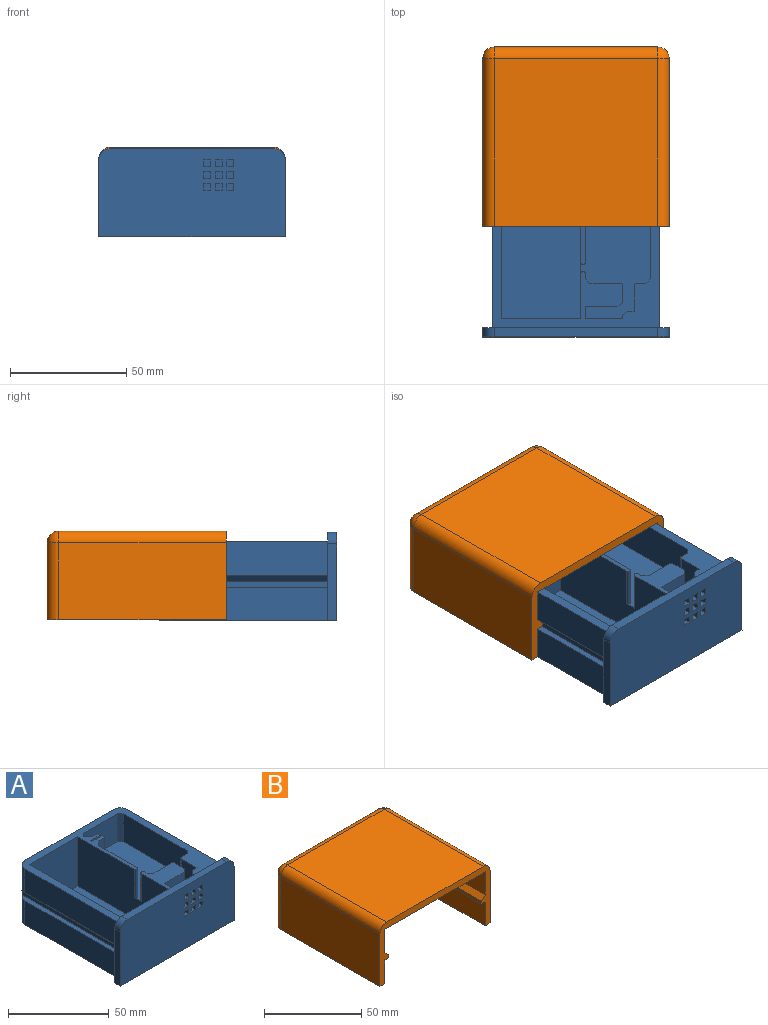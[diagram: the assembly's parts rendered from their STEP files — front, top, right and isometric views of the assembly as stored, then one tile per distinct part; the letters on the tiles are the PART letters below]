
ASSEMBLY  parts=2 mates=1
PART A: 96 faces, bbox 80x76x38 mm
  f0: plane 17x16mm, normal (0,1,0), area 191mm2, adj f11,f12,f34,f41,f42,f43,f44,f45
  f1: plane 80x38mm, normal (0,-1,0), area 2948.3mm2, adj f5,f6,f7,f8,f41,f42,f43,f44
  f2: plane 62x34mm, normal (0,1,0), area 2108mm2, adj f5,f34,f84,f85
  f3: plane 67x14.5mm, normal (-1,0,0), area 971.5mm2, adj f5,f37,f39,f84
  f4: plane 67x14.5mm, normal (1,0,0), area 971.5mm2, adj f5,f36,f39,f85
  f5: plane 80x76mm, normal (0,0,-1), area 5493.3mm2, adj f1,f2,f3,f4,f6,f8,f39,f84
  f6: plane 33x4mm, normal (1,0,0), area 132mm2, adj f1,f5,f39,f86
  f7: plane 70x4mm, normal (0,0,1), area 280mm2, adj f1,f39,f86,f87
  f8: plane 33x4mm, normal (-1,0,0), area 132mm2, adj f1,f5,f39,f87
  f9: plane 67x14.5mm, normal (-1,0,0), area 971.5mm2, adj f34,f39,f84,f94
  f10: plane 17x3mm, normal (0,1,0), area 51mm2, adj f32,f34,f77,f82
  f11: plane 17x1mm, normal (-1,0,0), area 17mm2, adj f0,f34,f77,f82
  f12: plane 17x5mm, normal (1,0,0), area 85mm2, adj f0,f13,f34,f77
  f13: plane 17x14mm, normal (0,-1,0), area 238mm2, adj f12,f34,f77,f81
  f14: plane 17x7mm, normal (1,0,0), area 119mm2, adj f34,f77,f81,f88
  f15: plane 17x13mm, normal (0,1,0), area 221mm2, adj f34,f77,f79,f88
  f16: plane 17x2mm, normal (1,0,0), area 34mm2, adj f34,f77,f79,f89
  f17: plane 64x30mm, normal (-1,0,0), area 1835mm2, adj f18,f20,f34,f40,f77,f89,f90
  f18: plane 34x30mm, normal (0,1,0), area 1020mm2, adj f17,f19,f34,f40
  f19: plane 64x30mm, normal (1,0,0), area 1920mm2, adj f18,f20,f34,f40
  f20: plane 34x30mm, normal (0,-1,0), area 1020mm2, adj f17,f19,f34,f40
  f21: plane 27x17mm, normal (1,0,0), area 459mm2, adj f34,f77,f90,f93
  f22: plane 17x4mm, normal (0,-1,0), area 68mm2, adj f23,f34,f77,f93
  f23: plane 17x2mm, normal (1,0,0), area 34mm2, adj f22,f24,f34,f77
  f24: plane 17x7mm, normal (0,1,0), area 119mm2, adj f23,f25,f34,f77
  f25: plane 17x1mm, normal (1,0,0), area 17mm2, adj f24,f26,f34,f77
  f26: plane 17x7mm, normal (0,-1,0), area 119mm2, adj f25,f27,f34,f77
  f27: plane 17x2mm, normal (1,0,0), area 34mm2, adj f26,f28,f34,f77
  f28: plane 17x4mm, normal (0,1,0), area 68mm2, adj f27,f34,f77,f92
  f29: plane 24x17mm, normal (0,-1,0), area 408mm2, adj f34,f77,f78,f83
  f30: plane 45x17mm, normal (-1,0,0), area 765mm2, adj f34,f77,f78,f80
  f31: plane 17x4mm, normal (0,1,0), area 68mm2, adj f34,f77,f80,f91
  f32: plane 17x11mm, normal (-1,0,0), area 187mm2, adj f10,f34,f77,f91
  f33: plane 67x14.5mm, normal (1,0,0), area 971.5mm2, adj f34,f39,f85,f95
  f34: plane 72x72mm, normal (0,0,1), area 1519mm2, adj f0,f2,f9,f10,f11,f12,f13,f14
  f35: plane 71.42x2.33mm, normal (1,0,0), area 166.7mm2, adj f36,f39,f85,f95
  f36: plane 71.42x2.67mm, normal (0,0,1), area 187.1mm2, adj f4,f35,f39,f85
  f37: plane 71.42x2.67mm, normal (0,0,1), area 187.1mm2, adj f3,f38,f39,f84
  f38: plane 71.42x2.33mm, normal (-1,0,0), area 166.7mm2, adj f37,f39,f84,f94
  f39: plane 80x38mm, normal (0,1,0), area 600.8mm2, adj f3,f4,f5,f6,f7,f8,f9,f33
  f40: plane 64x34mm, normal (0,0,1), area 2176mm2, adj f17,f18,f19,f20
  f41: plane 8x3mm, normal (0,0,-1), area 24mm2, adj f0,f1,f42,f44
  f42: plane 8x3mm, normal (-1,0,0), area 24mm2, adj f0,f1,f41,f43
  f43: plane 8x3mm, normal (0,0,1), area 24mm2, adj f0,f1,f42,f44
  f44: plane 8x3mm, normal (1,0,0), area 24mm2, adj f0,f1,f41,f43
  f45: plane 8x3mm, normal (0,0,-1), area 24mm2, adj f0,f1,f46,f48
  f46: plane 8x3mm, normal (-1,0,0), area 24mm2, adj f0,f1,f45,f47
  f47: plane 8x3mm, normal (0,0,1), area 24mm2, adj f0,f1,f46,f48
  f48: plane 8x3mm, normal (1,0,0), area 24mm2, adj f0,f1,f45,f47
  f49: plane 8x3mm, normal (0,0,-1), area 24mm2, adj f0,f1,f50,f52
  f50: plane 8x3mm, normal (-1,0,0), area 24mm2, adj f0,f1,f49,f51
  f51: plane 8x3mm, normal (0,0,1), area 24mm2, adj f0,f1,f50,f52
  f52: plane 8x3mm, normal (1,0,0), area 24mm2, adj f0,f1,f49,f51
  f53: plane 8x3mm, normal (0,0,-1), area 24mm2, adj f0,f1,f54,f55
  f54: plane 8x3mm, normal (1,0,0), area 24mm2, adj f0,f1,f53,f56
  f55: plane 8x3mm, normal (-1,0,0), area 24mm2, adj f0,f1,f53,f56
  f56: plane 8x3mm, normal (0,0,1), area 24mm2, adj f0,f1,f54,f55
  f57: plane 8x3mm, normal (0,0,-1), area 24mm2, adj f0,f1,f58,f60
  f58: plane 8x3mm, normal (-1,0,0), area 24mm2, adj f0,f1,f57,f59
  f59: plane 8x3mm, normal (0,0,1), area 24mm2, adj f0,f1,f58,f60
  f60: plane 8x3mm, normal (1,0,0), area 24mm2, adj f0,f1,f57,f59
  f61: plane 8x3mm, normal (0,0,-1), area 24mm2, adj f0,f1,f62,f63
  f62: plane 8x3mm, normal (1,0,0), area 24mm2, adj f0,f1,f61,f64
  f63: plane 8x3mm, normal (-1,0,0), area 24mm2, adj f0,f1,f61,f64
  f64: plane 8x3mm, normal (0,0,1), area 24mm2, adj f0,f1,f62,f63
  f65: plane 8x3mm, normal (0,0,-1), area 24mm2, adj f0,f1,f66,f68
  f66: plane 8x3mm, normal (-1,0,0), area 24mm2, adj f0,f1,f65,f67
  f67: plane 8x3mm, normal (0,0,1), area 24mm2, adj f0,f1,f66,f68
  f68: plane 8x3mm, normal (1,0,0), area 24mm2, adj f0,f1,f65,f67
  f69: plane 8x3mm, normal (-1,0,0), area 24mm2, adj f0,f1,f70,f72
  f70: plane 8x3mm, normal (0,0,1), area 24mm2, adj f0,f1,f69,f71
  f71: plane 8x3mm, normal (1,0,0), area 24mm2, adj f0,f1,f70,f72
  f72: plane 8x3mm, normal (0,0,-1), area 24mm2, adj f0,f1,f69,f71
  f73: plane 8x3mm, normal (-1,0,0), area 24mm2, adj f0,f1,f74,f76
  f74: plane 8x3mm, normal (0,0,1), area 24mm2, adj f0,f1,f73,f75
  f75: plane 8x3mm, normal (1,0,0), area 24mm2, adj f0,f1,f74,f76
  f76: plane 8x3mm, normal (0,0,-1), area 24mm2, adj f0,f1,f73,f75
  f77: plane 64x30mm, normal (0,0,1), area 1478.3mm2, adj f0,f10,f11,f12,f13,f14,f15,f16
  f78: plane 17x2mm, normal (-0.71,-0.71,0), area 48.1mm2, adj f29,f30,f34,f77
  f79: plane 17x2mm, normal (0.71,0.71,0), area 48.1mm2, adj f15,f16,f34,f77
  f80: plane 17x2mm, normal (-0.71,0.71,0), area 48.1mm2, adj f30,f31,f34,f77
  f81: plane 17x2mm, normal (0.71,-0.71,0), area 48.1mm2, adj f13,f14,f34,f77
  f82: plane 17x2mm, normal (-0.71,0.71,0), area 48.1mm2, adj f10,f11,f34,f77
  f83: plane 17x2mm, normal (0.71,-0.71,0), area 48.1mm2, adj f29,f34,f77,f92
  f84: cylinder r=5mm len=34mm, axis (0,0,-1), area 244.9mm2, adj f2,f3,f5,f9,f34,f37,f38,f94
  f85: cylinder r=5mm len=34mm, axis (0,0,1), area 244.9mm2, adj f2,f4,f5,f33,f34,f35,f36,f95
  f86: cylinder r=5mm len=5mm, axis (0,1,0), area 31.4mm2, adj f1,f6,f7,f39
  f87: cylinder r=5mm len=5mm, axis (0,1,0), area 31.4mm2, adj f1,f7,f8,f39
  f88: cylinder r=1mm len=17mm, axis (0,0,-1), area 26.7mm2, adj f14,f15,f34,f77
  f89: cylinder r=1mm len=17mm, axis (0,0,1), area 53.4mm2, adj f16,f17,f34,f77
  f90: cylinder r=1mm len=17mm, axis (0,0,1), area 53.4mm2, adj f17,f21,f34,f77
  f91: cylinder r=1mm len=17mm, axis (0,0,1), area 26.7mm2, adj f31,f32,f34,f77
  f92: plane 17x3mm, normal (0.71,0.71,0), area 72.1mm2, adj f28,f34,f77,f83
  f93: plane 17x3mm, normal (0.71,-0.71,0), area 72.1mm2, adj f21,f22,f34,f77
  f94: plane 71.42x2.67mm, normal (-0.71,0,-0.71), area 264.6mm2, adj f9,f38,f39,f84
  f95: plane 71.42x2.67mm, normal (0.71,0,-0.71), area 264.6mm2, adj f33,f35,f39,f85
PART B: 31 faces, bbox 80x77x38 mm
  f0: plane 80x77mm, normal (0,0,-1), area 922.4mm2, adj f1,f3,f5,f8,f9,f10,f14,f15
  f1: plane 80x38mm, normal (0,-1,0), area 570.6mm2, adj f0,f2,f3,f4,f5,f6,f7,f17
  f2: plane 72.8x72mm, normal (0,0,-1), area 5226.9mm2, adj f1,f8,f15,f16,f20,f23,f25,f27
  f3: plane 72x33mm, normal (1,0,0), area 2376mm2, adj f0,f1,f6,f10
  f4: plane 72x70mm, normal (0,0,1), area 5040mm2, adj f1,f6,f7,f12
  f5: plane 72x33mm, normal (-1,0,0), area 2376mm2, adj f0,f1,f7,f14
  f6: cylinder r=5mm len=72mm, axis (0,-1,0), area 565.5mm2, adj f1,f3,f4,f11
  f7: cylinder r=5mm len=72mm, axis (0,-1,0), area 565.5mm2, adj f1,f4,f5,f13
  f8: plane 62x34mm, normal (0,-1,0), area 2108mm2, adj f0,f2,f15,f16
  f9: plane 70x33mm, normal (0,1,0), area 2310mm2, adj f0,f10,f12,f14
  f10: cylinder r=5mm len=33mm, axis (0,0,-1), area 259.2mm2, adj f0,f3,f9,f11
  f11: sphere r=5mm, area 39.3mm2, adj f6,f10,f12
  f12: cylinder r=5mm len=70mm, axis (1,0,0), area 549.8mm2, adj f4,f9,f11,f13
  f13: sphere r=5mm, area 39.3mm2, adj f7,f12,f14
  f14: cylinder r=5mm len=33mm, axis (0,0,1), area 259.2mm2, adj f0,f5,f9,f13
  f15: cylinder r=5mm len=34mm, axis (0,0,-1), area 250.9mm2, adj f0,f2,f8,f17,f18,f19,f22,f23
  f16: cylinder r=5mm len=34mm, axis (0,0,1), area 250.9mm2, adj f0,f2,f8,f24,f25,f28,f29,f30
  f17: plane 71.19x2.67mm, normal (0.71,0,0.71), area 262.1mm2, adj f1,f15,f18,f20,f23
  f18: plane 71.19x1.77mm, normal (1,0,0), area 125.8mm2, adj f1,f15,f17,f19
  f19: plane 71.19x2.67mm, normal (0,0,-1), area 185.4mm2, adj f1,f15,f18,f21,f22
  f20: plane 67x14.67mm, normal (1,0,0), area 982.6mm2, adj f1,f2,f17,f23
  f21: plane 67x14.9mm, normal (1,0,0), area 998.3mm2, adj f0,f1,f19,f22
  f22: plane 14.9x0.4mm, normal (0,-1,0), area 6mm2, adj f0,f15,f19,f21
  f23: plane 15.07x0.4mm, normal (0,-1,0), area 5.9mm2, adj f2,f15,f17,f20
  f24: plane 14.9x0.4mm, normal (0,-1,0), area 6mm2, adj f0,f16,f26,f29
  f25: plane 15.07x0.4mm, normal (0,-1,0), area 5.9mm2, adj f2,f16,f27,f30
  f26: plane 67x14.9mm, normal (-1,0,0), area 998.3mm2, adj f0,f1,f24,f29
  f27: plane 67x14.67mm, normal (-1,0,0), area 982.6mm2, adj f1,f2,f25,f30
  f28: plane 71.19x1.77mm, normal (-1,0,0), area 125.8mm2, adj f1,f16,f29,f30
  f29: plane 71.19x2.67mm, normal (0,0,-1), area 185.4mm2, adj f1,f16,f24,f26,f28
  f30: plane 71.19x2.67mm, normal (-0.71,0,0.71), area 262.1mm2, adj f1,f16,f25,f27,f28
PLACE A rot(axis=(-0.72,-0.35,0.61),0deg) t=(36.59,-31.8,-29.61)mm
PLACE B t=(36.59,11.68,-29.11)mm
MATE slider B.f9 <-> A.f2  axis (0,1,0) through (16.59,79.68,-16.61)mm
